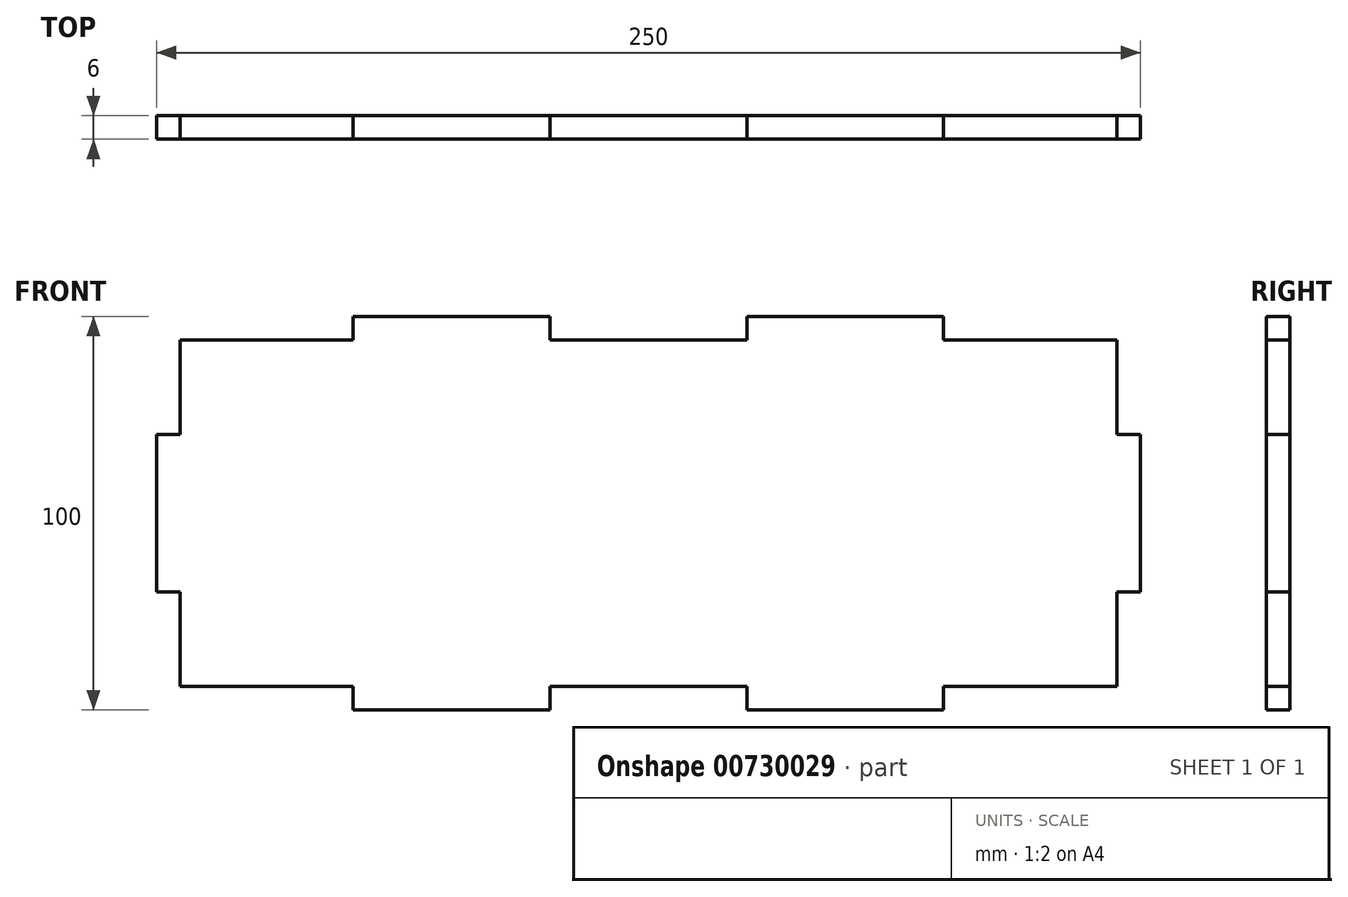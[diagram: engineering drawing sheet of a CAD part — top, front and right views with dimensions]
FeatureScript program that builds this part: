
annotation { "Feature Type Name" : "Feature", "Feature Type Description" : "" }
export const myFeature = defineFeature(function(context is Context, id is Id, definition is map)
    precondition{}
    {
        {
            var Q0;
            Q0=qCreatedBy(makeId("Front.planeOp"),FACE);
            var sketch = newSketch(context, id + "F0", { "sketchPlane" : qUnion([Q0])});
            skLineSegment(sketch, "E0", {"start": v(-64.49, -34.79) * mm, "end": v(-20.49, -34.79) * mm});
            skLineSegment(sketch, "E1", {"start": v(-20.49, -34.79) * mm, "end": v(-20.49, -40.79) * mm});
            skLineSegment(sketch, "E2", {"start": v(-20.49, -40.79) * mm, "end": v(29.51, -40.79) * mm});
            skLineSegment(sketch, "E3", {"start": v(29.51, -40.79) * mm, "end": v(29.51, -34.79) * mm});
            skLineSegment(sketch, "E4", {"start": v(29.51, -34.79) * mm, "end": v(79.51, -34.79) * mm});
            skLineSegment(sketch, "E5", {"start": v(79.51, -34.79) * mm, "end": v(79.51, -40.79) * mm});
            skLineSegment(sketch, "E6", {"start": v(79.51, -40.79) * mm, "end": v(129.51, -40.79) * mm});
            skLineSegment(sketch, "E7", {"start": v(129.51, -40.79) * mm, "end": v(129.51, -34.79) * mm});
            skLineSegment(sketch, "E8", {"start": v(129.51, -34.79) * mm, "end": v(173.51, -34.79) * mm});
            skLineSegment(sketch, "E9", {"start": v(173.51, -34.79) * mm, "end": v(173.51, -10.79) * mm});
            skLineSegment(sketch, "E10", {"start": v(173.51, -10.79) * mm, "end": v(179.51, -10.79) * mm});
            skLineSegment(sketch, "E11", {"start": v(179.51, -10.79) * mm, "end": v(179.51, 29.21) * mm});
            skLineSegment(sketch, "E12", {"start": v(179.51, 29.21) * mm, "end": v(173.51, 29.21) * mm});
            skLineSegment(sketch, "E13", {"start": v(173.51, 29.21) * mm, "end": v(173.51, 53.21) * mm});
            skLineSegment(sketch, "E14", {"start": v(173.51, 53.21) * mm, "end": v(129.51, 53.21) * mm});
            skLineSegment(sketch, "E15", {"start": v(129.51, 53.21) * mm, "end": v(129.51, 59.21) * mm});
            skLineSegment(sketch, "E16", {"start": v(129.51, 59.21) * mm, "end": v(79.51, 59.21) * mm});
            skLineSegment(sketch, "E17", {"start": v(79.51, 59.21) * mm, "end": v(79.51, 53.21) * mm});
            skLineSegment(sketch, "E18", {"start": v(79.51, 53.21) * mm, "end": v(29.51, 53.21) * mm});
            skLineSegment(sketch, "E19", {"start": v(29.51, 53.21) * mm, "end": v(29.51, 59.21) * mm});
            skLineSegment(sketch, "E20", {"start": v(29.51, 59.21) * mm, "end": v(-20.49, 59.21) * mm});
            skLineSegment(sketch, "E21", {"start": v(-20.49, 59.21) * mm, "end": v(-20.49, 53.21) * mm});
            skLineSegment(sketch, "E22", {"start": v(-20.49, 53.21) * mm, "end": v(-64.49, 53.21) * mm});
            skLineSegment(sketch, "E23", {"start": v(-64.49, 53.21) * mm, "end": v(-64.49, 29.21) * mm});
            skLineSegment(sketch, "E24", {"start": v(-64.49, 29.21) * mm, "end": v(-70.49, 29.21) * mm});
            skLineSegment(sketch, "E25", {"start": v(-70.49, 29.21) * mm, "end": v(-70.49, -10.79) * mm});
            skLineSegment(sketch, "E26", {"start": v(-70.49, -10.79) * mm, "end": v(-64.49, -10.79) * mm});
            skLineSegment(sketch, "E27", {"start": v(-64.49, -10.79) * mm, "end": v(-64.49, -34.79) * mm});
            skSolve(sketch);
        }
        {
            var Q0;
            Q0 = qSketchRegion(id + "F0", true);
            extrude(context, id + "F1", {"entities" : qUnion([Q0]), "depth" : 6 * mm, "offsetDistance" : 25 * mm});
        }
    });
